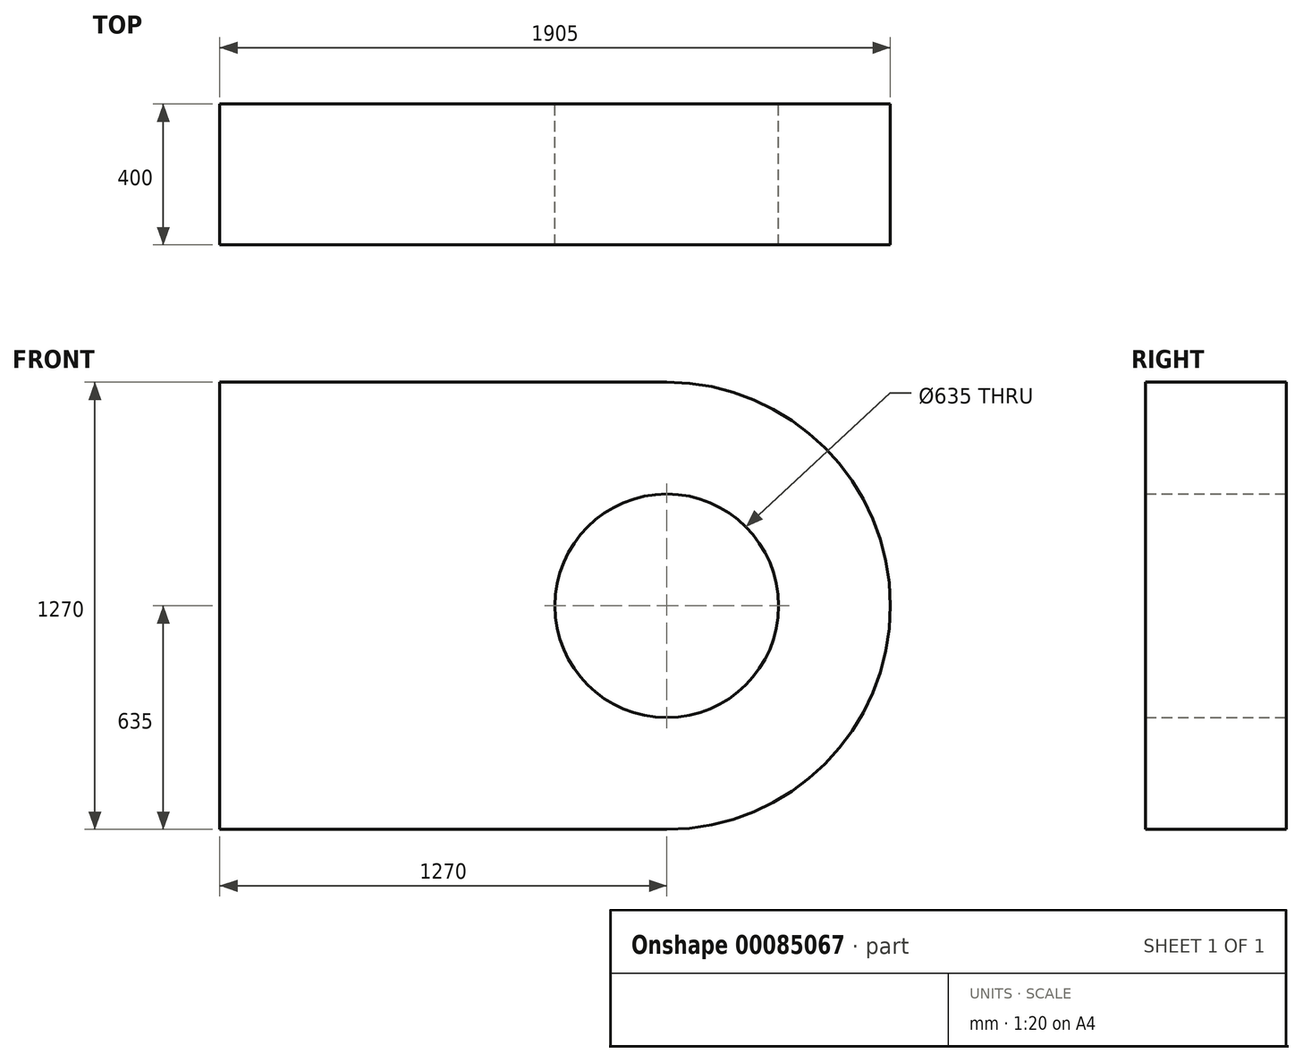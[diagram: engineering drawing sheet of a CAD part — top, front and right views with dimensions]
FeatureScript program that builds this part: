
annotation { "Feature Type Name" : "Feature", "Feature Type Description" : "" }
export const myFeature = defineFeature(function(context is Context, id is Id, definition is map)
    precondition{}
    {
        {
            var Q0;
            Q0=qCreatedBy(makeId("Front.planeOp"),FACE);
            var sketch = newSketch(context, id + "F0", { "sketchPlane" : qUnion([Q0])});
            skArc(sketch, "E0", {"start": v(0, -635) * mm, "mid": v(635, 0) * mm, "end": v(0, 635) * mm});
            skLineSegment(sketch, "E1", {"start": v(0, 635) * mm, "end": v(-1270, 635) * mm});
            skLineSegment(sketch, "E2", {"start": v(-1270, 635) * mm, "end": v(-1270, -635) * mm});
            skLineSegment(sketch, "E3", {"start": v(-1270, -635) * mm, "end": v(0, -635) * mm});
            skCircle(sketch, "E4", {"center": v(0, 0) * mm, "radius": 317.5 * mm});
            skSolve(sketch);
        }
        {
            var Q0;
            Q0=makeQuery(id+"F0.imprint","IMPRINT",FACE,{"disambiguationData":[TD([[makeQuery(id+"F0.imprint","IMPRINT",EDGE,{"derivedFrom":sQuery(id+"F0.wireOp",EDGE,"E0")}),1.0]])]});
            extrude(context, id + "F1", {"entities" : qUnion([Q0]), "depth" : 400 * mm});
        }
    });
